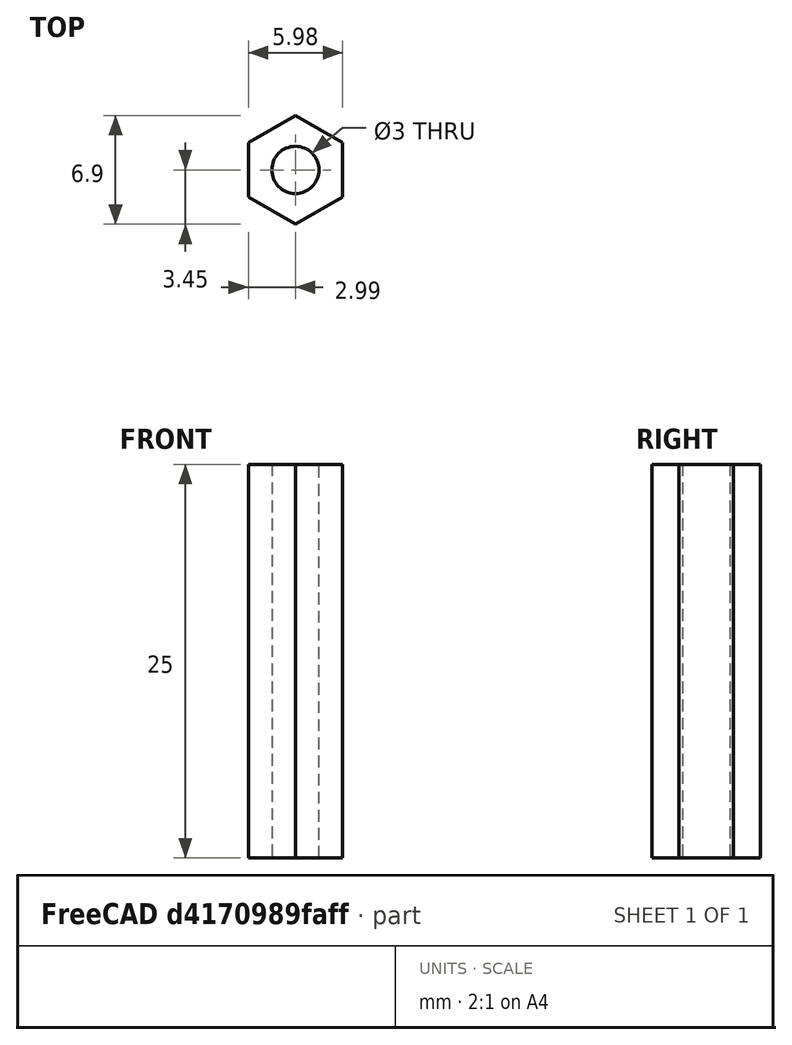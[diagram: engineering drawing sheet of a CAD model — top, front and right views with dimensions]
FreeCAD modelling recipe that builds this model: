
FCSTD DOCUMENT  (FreeCAD 0.16R6704 (Git))
Label: spacer-M3-25
License: All rights reserved
LicenseURL: http://en.wikipedia.org/wiki/All_rights_reserved
objects: Sketcher::SketchObject×1, PartDesign::Pad×1
note: 3 computed .brp shape members not serialized (recipe doc carries the construction recipe); baked Part::Feature solids carry a one-line shape summary decoded from their .brp

FEATURE [Sketcher::SketchObject] Sketch
  sketch-geometry (8):
    g0: LineSegment StartX=0 StartY=3.45 StartZ=0 EndX=-2.98779 EndY=1.725 EndZ=0
    g1: LineSegment StartX=-2.98779 StartY=1.725 StartZ=0 EndX=-2.98779 EndY=-1.725 EndZ=0
    g2: LineSegment StartX=-2.98779 StartY=-1.725 StartZ=0 EndX=0 EndY=-3.45 EndZ=0
    g3: LineSegment StartX=0 StartY=-3.45 StartZ=0 EndX=2.98779 EndY=-1.725 EndZ=0
    g4: LineSegment StartX=2.98779 StartY=-1.725 StartZ=0 EndX=2.98779 EndY=1.725 EndZ=0
    g5: LineSegment StartX=2.98779 StartY=1.725 StartZ=0 EndX=0 EndY=3.45 EndZ=0
    g6: Circle [constr] CenterX=0 CenterY=0 CenterZ=0 NormalX=0 NormalY=0 NormalZ=1 Radius=3.45
    g7: Circle CenterX=0 CenterY=0 CenterZ=0 NormalX=0 NormalY=0 NormalZ=1 Radius=1.5
  constraints (18):
    c: Coincident(g0,g1)
    c: Coincident(g1,g2)
    c: Coincident(g2,g3)
    c: Coincident(g3,g4)
    c: Coincident(g4,g5)
    c: Coincident(g5,g0)
    c: Equal(g0, g1-g5) x5
    c: PointOnObject(g0,g6)
    c: PointOnObject(g1,g6)
    c: PointOnObject(g2,g6)
    c: PointOnObject(g3,g6)
    c: PointOnObject(g4,g6)
    c: PointOnObject(g5,g6)
    c: Coincident(g6,g-1)
    c: Vertical(g1)
    c: DistanceY(g2,g0) = 6.9
    c: Coincident(g7,g-1)
    c: Radius(g7) = 1.5
FEATURE [PartDesign::Pad] Pad
  Length = 25
  Length2 = 100
  Sketch = -> Sketch
  Type = 0
